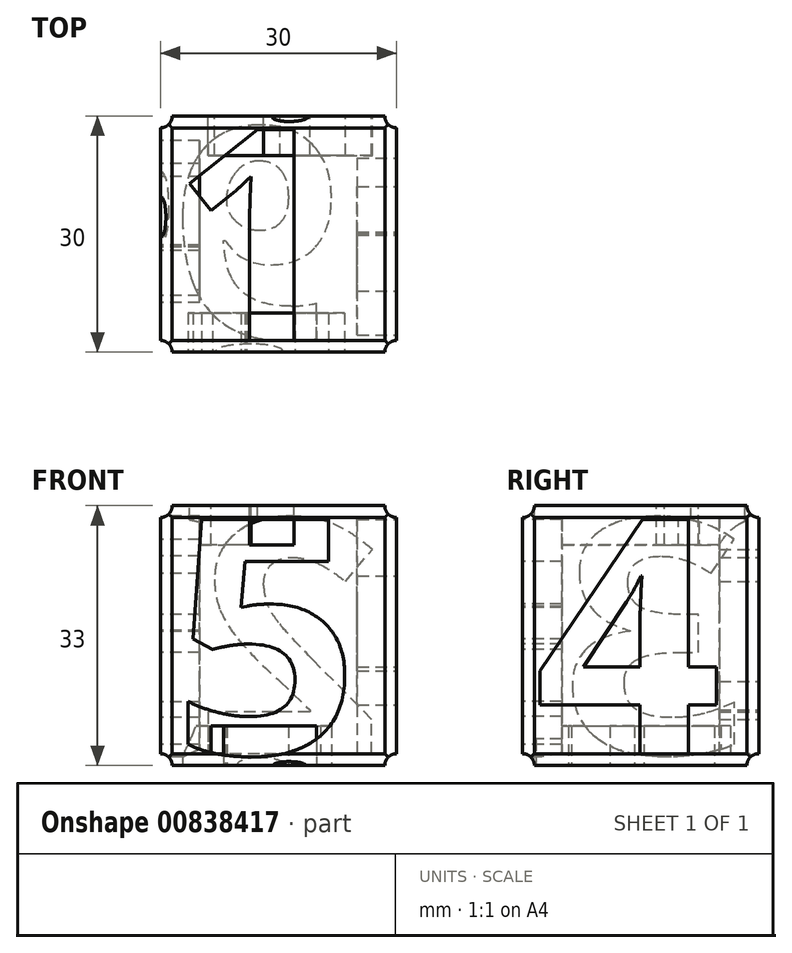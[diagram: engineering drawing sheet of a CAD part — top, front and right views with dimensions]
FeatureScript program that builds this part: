
annotation { "Feature Type Name" : "Feature", "Feature Type Description" : "" }
export const myFeature = defineFeature(function(context is Context, id is Id, definition is map)
    precondition{}
    {
        {
            var Q0;
            Q0=qCreatedBy(makeId("Top.planeOp"),FACE);
            var sketch = newSketch(context, id + "F0", { "sketchPlane" : qUnion([Q0])});
            skLineSegment(sketch, "E0.bottom", {"start": v(1.5, 0) * mm, "end": v(28.5, 0) * mm});
            skLineSegment(sketch, "E0.top", {"start": v(1.5, 30) * mm, "end": v(28.5, 30) * mm});
            skLineSegment(sketch, "E0.left", {"start": v(0, 1.5) * mm, "end": v(0, 28.5) * mm});
            skLineSegment(sketch, "E0.right", {"start": v(30, 1.5) * mm, "end": v(30, 28.5) * mm});
            skArc(sketch, "E1", {"start": v(0, 28.5) * mm, "mid": v(1.06, 28.94) * mm, "end": v(1.5, 30) * mm});
            skArc(sketch, "E2", {"start": v(28.5, 30) * mm, "mid": v(28.94, 28.94) * mm, "end": v(30, 28.5) * mm});
            skArc(sketch, "E3", {"start": v(30, 1.5) * mm, "mid": v(28.94, 1.06) * mm, "end": v(28.5, 0) * mm});
            skArc(sketch, "E4", {"start": v(1.5, 0) * mm, "mid": v(1.06, 1.06) * mm, "end": v(0, 1.5) * mm});
            skSolve(sketch);
        }
        {
            var Q0;
            Q0=makeQuery(id+"F0.imprint","IMPRINT",FACE,{"disambiguationData":[TD([[makeQuery(id+"F0.imprint","IMPRINT",EDGE,{"derivedFrom":sQuery(id+"F0.wireOp",EDGE,"E0.bottom")}),1.0]])]});
            extrude(context, id + "F1", {"entities" : qUnion([Q0]), "depth" : 33 * mm, "offsetDistance" : 25 * mm});
        }
        {
            var Q0;
            Q0=qCreatedBy(makeId("Right.planeOp"),FACE);
            var sketch = newSketch(context, id + "F2", { "sketchPlane" : qUnion([Q0])});
            skCircle(sketch, "E5", {"center": v(0, 33) * mm, "radius": 1.5 * mm});
            skSolve(sketch);
        }
        {
            var Q0;
            Q0 = qSketchRegion(id + "F2", true);
            extrude(context, id + "F3", {"entities" : qUnion([Q0]), "operationType" : NewBodyOperationType.REMOVE, "endBound" : BoundingType.THROUGH_ALL, "depth" : 25 * mm, "offsetDistance" : 25 * mm});
        }
        {
            var Q0;
            Q0=qCreatedBy(makeId("Front.planeOp"),FACE);
            var sketch = newSketch(context, id + "F4", { "sketchPlane" : qUnion([Q0])});
            skCircle(sketch, "E6", {"center": v(30, 33) * mm, "radius": 1.5 * mm});
            skSolve(sketch);
        }
        {
            var Q0;
            Q0=makeQuery(id+"F4.imprint","IMPRINT",FACE,{"disambiguationData":[TD([[makeQuery(id+"F4.imprint","IMPRINT",EDGE,{"derivedFrom":sQuery(id+"F4.wireOp",EDGE,"E6")}),1.0]])]});
            var Q1;
            Q1 = qConstructionFilter(qBodyType(qCreatedBy(id + "F4" ,EDGE), BodyType.WIRE), ConstructionObject.NO);
            extrude(context, id + "F5", {"entities" : qUnion([Q0]), "operationType" : NewBodyOperationType.REMOVE, "surfaceEntities" : qUnion([Q1]), "endBound" : BoundingType.THROUGH_ALL, "oppositeDirection" : true, "depth" : 25 * mm, "offsetDistance" : 25 * mm});
        }
        {
            var Q0;
            Q0=qCreatedBy(makeId("Right.planeOp"),FACE);
            var sketch = newSketch(context, id + "F6", { "sketchPlane" : qUnion([Q0])});
            skCircle(sketch, "E7", {"center": v(0, 0) * mm, "radius": 1.5 * mm});
            skCircle(sketch, "E8", {"center": v(30, 0) * mm, "radius": 1.5 * mm});
            skSolve(sketch);
        }
        {
            var Q0;
            Q0 = qSketchRegion(id + "F6", true);
            extrude(context, id + "F7", {"entities" : qUnion([Q0]), "operationType" : NewBodyOperationType.REMOVE, "endBound" : BoundingType.THROUGH_ALL, "depth" : 25 * mm, "offsetDistance" : 25 * mm});
        }
        {
            var Q0;
            Q0=qCreatedBy(makeId("Right.planeOp"),FACE);
            var sketch = newSketch(context, id + "F8", { "sketchPlane" : qUnion([Q0])});
            skCircle(sketch, "E9", {"center": v(30, 33) * mm, "radius": 1.5 * mm});
            skSolve(sketch);
        }
        {
            var Q0;
            Q0 = qSketchRegion(id + "F8", true);
            extrude(context, id + "F9", {"entities" : qUnion([Q0]), "operationType" : NewBodyOperationType.REMOVE, "endBound" : BoundingType.THROUGH_ALL, "depth" : 25 * mm, "offsetDistance" : 25 * mm});
        }
        {
            var Q0;
            Q0=qCreatedBy(makeId("Front.planeOp"),FACE);
            var sketch = newSketch(context, id + "F10", { "sketchPlane" : qUnion([Q0])});
            skCircle(sketch, "E10", {"center": v(30, 0) * mm, "radius": 1.5 * mm});
            skCircle(sketch, "E11", {"center": v(0, 0) * mm, "radius": 1.5 * mm});
            skSolve(sketch);
        }
        {
            var Q0;
            Q0 = qSketchRegion(id + "F10", true);
            extrude(context, id + "F11", {"entities" : qUnion([Q0]), "operationType" : NewBodyOperationType.REMOVE, "endBound" : BoundingType.THROUGH_ALL, "oppositeDirection" : true, "depth" : 25 * mm, "offsetDistance" : 25 * mm});
        }
        {
            var Q0;
            Q0=qCreatedBy(makeId("Front.planeOp"),FACE);
            var sketch = newSketch(context, id + "F12", { "sketchPlane" : qUnion([Q0])});
            skCircle(sketch, "E12", {"center": v(0, 33) * mm, "radius": 1.5 * mm});
            skSolve(sketch);
        }
        {
            var Q0;
            Q0 = qSketchRegion(id + "F12", true);
            extrude(context, id + "F13", {"entities" : qUnion([Q0]), "operationType" : NewBodyOperationType.REMOVE, "endBound" : BoundingType.THROUGH_ALL, "oppositeDirection" : true, "depth" : 25 * mm, "offsetDistance" : 25 * mm});
        }
        {
            var Q0;
            Q0=makeQuery(id+"F1.opExtrude","CAP_FACE",FACE,{"disambiguationData":[OSD([sQuery(id+"F0.wireOp",EDGE,"E0.bottom"),sQuery(id+"F0.wireOp",EDGE,"E0.top"),sQuery(id+"F0.wireOp",EDGE,"E0.left"),sQuery(id+"F0.wireOp",EDGE,"E0.right"),sQuery(id+"F0.wireOp",EDGE,"E1"),sQuery(id+"F0.wireOp",EDGE,"E2"),sQuery(id+"F0.wireOp",EDGE,"E3"),sQuery(id+"F0.wireOp",EDGE,"E4")])],"isStart":false});
            var sketch = newSketch(context, id + "F14", { "sketchPlane" : qUnion([Q0])});
            skText(sketch, "E13", { "text": "1", "fontName": "OpenSans-Bold.ttf"});
            const initialGuessF14  = {"E13": [0.0015, 0.0015, 1, 0, 0.027]};
            skSetInitialGuess(sketch, initialGuessF14);
            skSolve(sketch);
        }
        {
            var Q0;
            Q0 = qSketchRegion(id + "F14", true);
            extrude(context, id + "F15", {"entities" : qUnion([Q0]), "operationType" : NewBodyOperationType.REMOVE, "oppositeDirection" : true, "depth" : 5 * mm, "offsetDistance" : 25 * mm});
        }
        {
            var Q0;
            Q0=makeQuery(id+"F1.opExtrude","CAP_FACE",FACE,{"disambiguationData":[OSD([sQuery(id+"F0.wireOp",EDGE,"E0.bottom"),sQuery(id+"F0.wireOp",EDGE,"E0.top"),sQuery(id+"F0.wireOp",EDGE,"E0.left"),sQuery(id+"F0.wireOp",EDGE,"E0.right"),sQuery(id+"F0.wireOp",EDGE,"E1"),sQuery(id+"F0.wireOp",EDGE,"E2"),sQuery(id+"F0.wireOp",EDGE,"E3"),sQuery(id+"F0.wireOp",EDGE,"E4")])],"isStart":true});
            var sketch = newSketch(context, id + "F16", { "sketchPlane" : qUnion([Q0])});
            skText(sketch, "E14", { "text": "6", "fontName": "OpenSans-Bold.ttf"});
            const initialGuessF16  = {"E14": [0.0015, -0.0285, 1, 0, 0.027]};
            skSetInitialGuess(sketch, initialGuessF16);
            skSolve(sketch);
        }
        {
            var Q0;
            Q0 = qSketchRegion(id + "F16", true);
            extrude(context, id + "F17", {"entities" : qUnion([Q0]), "operationType" : NewBodyOperationType.REMOVE, "oppositeDirection" : true, "depth" : 5 * mm, "offsetDistance" : 25 * mm});
        }
        {
            var Q0;
            Q0=makeQuery(id+"F1.opExtrude","SWEPT_FACE",FACE,{"disambiguationData":[OSD([sQuery(id+"F0.wireOp",EDGE,"E0.right")])]});
            var sketch = newSketch(context, id + "F18", { "sketchPlane" : qUnion([Q0])});
            skText(sketch, "E15", { "text": "4", "fontName": "OpenSans-Bold.ttf"});
            const initialGuessF18  = {"E15": [0.0015, 0.0015, 1, 0, 0.03]};
            skSetInitialGuess(sketch, initialGuessF18);
            skSolve(sketch);
        }
        {
            var Q0;
            Q0 = qSketchRegion(id + "F18", true);
            extrude(context, id + "F19", {"entities" : qUnion([Q0]), "operationType" : NewBodyOperationType.REMOVE, "oppositeDirection" : true, "depth" : 5 * mm, "offsetDistance" : 25 * mm});
        }
        {
            var Q0;
            Q0=makeQuery(id+"F1.opExtrude","SWEPT_FACE",FACE,{"disambiguationData":[OSD([sQuery(id+"F0.wireOp",EDGE,"E0.left")])]});
            var sketch = newSketch(context, id + "F20", { "sketchPlane" : qUnion([Q0])});
            skText(sketch, "E16", { "text": "3", "fontName": "OpenSans-Bold.ttf"});
            const initialGuessF20  = {"E16": [-0.0285, 0.0015, 1, 0, 0.03]};
            skSetInitialGuess(sketch, initialGuessF20);
            skSolve(sketch);
        }
        {
            var Q0;
            Q0 = qSketchRegion(id + "F20", true);
            extrude(context, id + "F21", {"entities" : qUnion([Q0]), "operationType" : NewBodyOperationType.REMOVE, "oppositeDirection" : true, "depth" : 5 * mm, "offsetDistance" : 25 * mm});
        }
        {
            var Q0;
            Q0=makeQuery(id+"F1.opExtrude","SWEPT_FACE",FACE,{"disambiguationData":[OSD([sQuery(id+"F0.wireOp",EDGE,"E0.bottom")])]});
            var sketch = newSketch(context, id + "F22", { "sketchPlane" : qUnion([Q0])});
            skText(sketch, "E17", { "text": "5", "fontName": "OpenSans-Bold.ttf"});
            const initialGuessF22  = {"E17": [0.0015, 0.0015, 1, 0, 0.03]};
            skSetInitialGuess(sketch, initialGuessF22);
            skSolve(sketch);
        }
        {
            var Q0;
            Q0 = qSketchRegion(id + "F22", true);
            extrude(context, id + "F23", {"entities" : qUnion([Q0]), "operationType" : NewBodyOperationType.REMOVE, "oppositeDirection" : true, "depth" : 5 * mm, "offsetDistance" : 25 * mm});
        }
        {
            var Q0;
            Q0=makeQuery(id+"F1.opExtrude","SWEPT_FACE",FACE,{"disambiguationData":[OSD([sQuery(id+"F0.wireOp",EDGE,"E0.top")])]});
            var sketch = newSketch(context, id + "F24", { "sketchPlane" : qUnion([Q0])});
            skText(sketch, "E18", { "text": "2", "fontName": "OpenSans-Bold.ttf"});
            const initialGuessF24  = {"E18": [-0.0285, 0.0015, 1, 0, 0.03]};
            skSetInitialGuess(sketch, initialGuessF24);
            skSolve(sketch);
        }
        {
            var Q0;
            Q0 = qSketchRegion(id + "F24", true);
            extrude(context, id + "F25", {"entities" : qUnion([Q0]), "operationType" : NewBodyOperationType.REMOVE, "oppositeDirection" : true, "depth" : 5 * mm, "offsetDistance" : 25 * mm});
        }
    });
